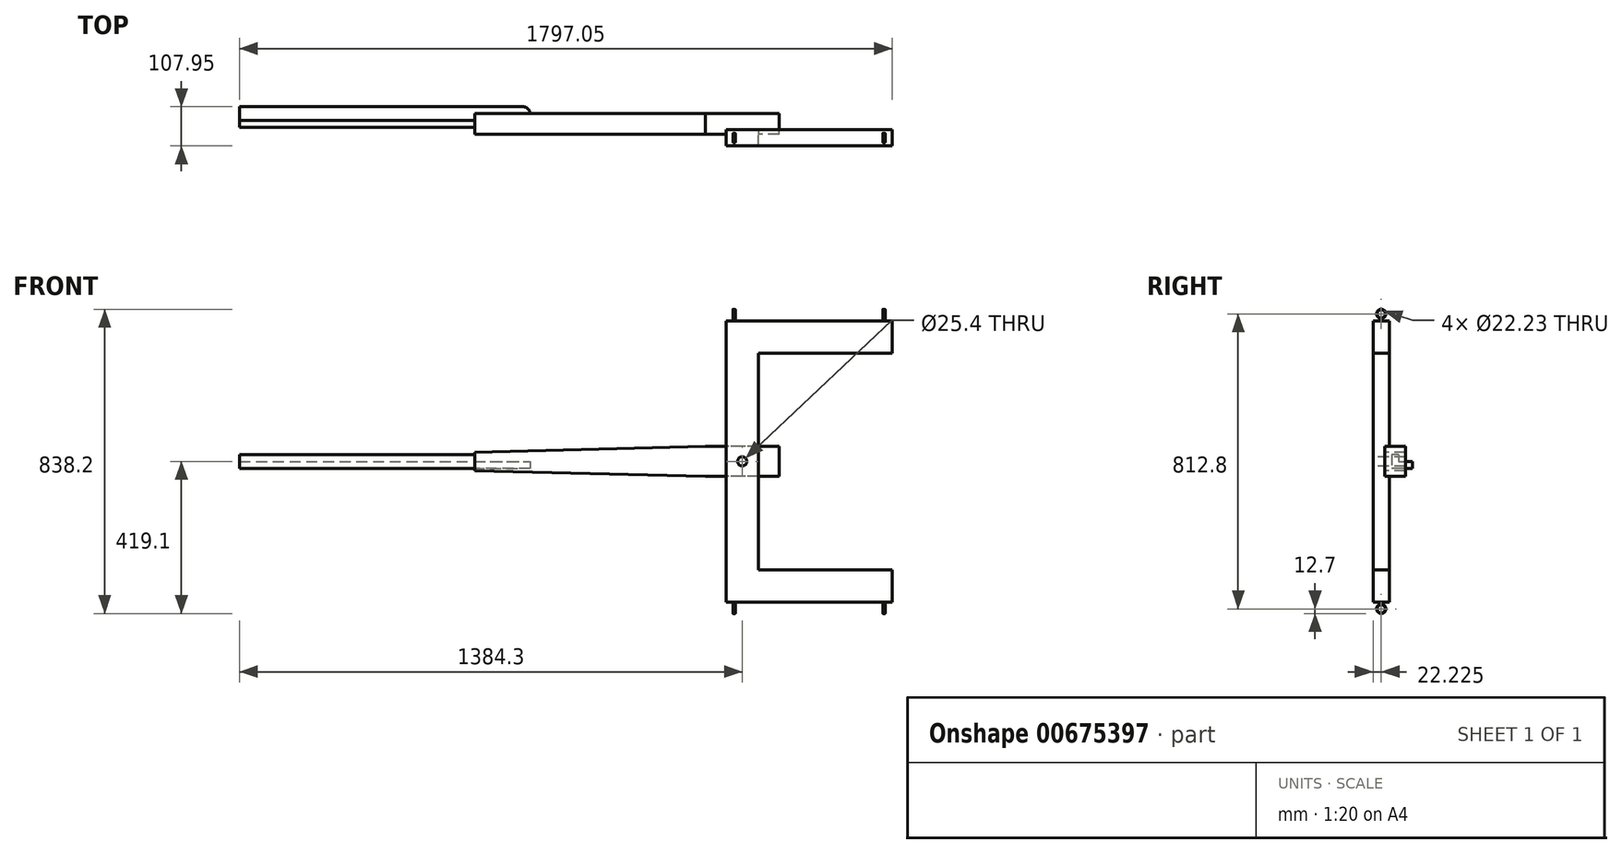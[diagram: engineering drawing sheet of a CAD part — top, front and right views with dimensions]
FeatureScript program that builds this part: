
annotation { "Feature Type Name" : "Feature", "Feature Type Description" : "" }
export const myFeature = defineFeature(function(context is Context, id is Id, definition is map)
    precondition{}
    {
        {
            var Q0;
            Q0=qCreatedBy(makeId("Front.planeOp"),FACE);
            var sketch = newSketch(context, id + "F0", { "sketchPlane" : qUnion([Q0])});
            skLineSegment(sketch, "E0.bottom", {"start": v(101.6, 41.27) * mm, "end": v(-736.6, 41.27) * mm});
            skLineSegment(sketch, "E0.top", {"start": v(101.6, -41.27) * mm, "end": v(-736.6, -41.28) * mm});
            skLineSegment(sketch, "E0.left", {"start": v(101.6, 41.28) * mm, "end": v(101.6, -41.27) * mm});
            skLineSegment(sketch, "E0.right", {"start": v(-736.6, 41.27) * mm, "end": v(-736.6, -41.28) * mm});
            skSolve(sketch);
        }
        {
            var Q0;
            Q0 = qSketchRegion(id + "F0", true);
            extrude(context, id + "F1", {"entities" : qUnion([Q0]), "depth" : 57.15 * mm, "offsetDistance" : 25.4 * mm});
        }
        {
            var Q0;
            Q0=makeQuery(id+"F1.opExtrude","CAP_FACE",FACE,{"disambiguationData":[OSD([sQuery(id+"F0.wireOp",EDGE,"E0.bottom"),sQuery(id+"F0.wireOp",EDGE,"E0.top"),sQuery(id+"F0.wireOp",EDGE,"E0.left"),sQuery(id+"F0.wireOp",EDGE,"E0.right")])],"isStart":false});
            var sketch = newSketch(context, id + "F2", { "sketchPlane" : qUnion([Q0])});
            skLineSegment(sketch, "E1", {"start": v(-736.6, 41.27) * mm, "end": v(-736.6, 25.4) * mm});
            skLineSegment(sketch, "E2", {"start": v(-736.6, 25.4) * mm, "end": v(-101.6, 41.27) * mm});
            skLineSegment(sketch, "E3", {"start": v(-101.6, 41.27) * mm, "end": v(-736.6, 41.27) * mm});
            skLineSegment(sketch, "E4", {"start": v(-736.6, -41.28) * mm, "end": v(-736.6, -25.4) * mm});
            skLineSegment(sketch, "E5", {"start": v(-736.6, -25.4) * mm, "end": v(-101.6, -41.27) * mm});
            skLineSegment(sketch, "E6", {"start": v(-101.6, -41.28) * mm, "end": v(-736.6, -41.28) * mm});
            skSolve(sketch);
        }
        {
            var Q0;
            Q0 = qSketchRegion(id + "F2", true);
            extrude(context, id + "F3", {"entities" : qUnion([Q0]), "operationType" : NewBodyOperationType.REMOVE, "endBound" : BoundingType.THROUGH_ALL, "oppositeDirection" : true, "depth" : 25.4 * mm, "offsetDistance" : 25.4 * mm});
        }
        {
            var Q0;
            Q0=makeQuery(id+"F1.opExtrude","CAP_FACE",FACE,{"disambiguationData":[OSD([sQuery(id+"F0.wireOp",EDGE,"E0.bottom"),sQuery(id+"F0.wireOp",EDGE,"E0.top"),sQuery(id+"F0.wireOp",EDGE,"E0.left"),sQuery(id+"F0.wireOp",EDGE,"E0.right")])],"isStart":false});
            var sketch = newSketch(context, id + "F4", { "sketchPlane" : qUnion([Q0])});
            skLineSegment(sketch, "E7.left", {"start": v(-44.45, 298.45) * mm, "end": v(-44.45, -298.45) * mm});
            skLineSegment(sketch, "E7.right", {"start": v(44.45, 298.45) * mm, "end": v(44.45, -298.45) * mm});
            skLineSegment(sketch, "E8.bottom", {"start": v(44.45, 298.45) * mm, "end": v(412.75, 298.45) * mm});
            skLineSegment(sketch, "E8.top", {"start": v(-44.45, 387.35) * mm, "end": v(412.75, 387.35) * mm});
            skLineSegment(sketch, "E8.left", {"start": v(-44.45, 298.45) * mm, "end": v(-44.45, 387.35) * mm});
            skLineSegment(sketch, "E8.right", {"start": v(412.75, 298.45) * mm, "end": v(412.75, 387.35) * mm});
            skLineSegment(sketch, "E9.bottom", {"start": v(44.45, -298.45) * mm, "end": v(412.75, -298.45) * mm});
            skLineSegment(sketch, "E9.top", {"start": v(-44.45, -387.35) * mm, "end": v(412.75, -387.35) * mm});
            skLineSegment(sketch, "E9.left", {"start": v(-44.45, -298.45) * mm, "end": v(-44.45, -387.35) * mm});
            skLineSegment(sketch, "E9.right", {"start": v(412.75, -298.45) * mm, "end": v(412.75, -387.35) * mm});
            skSolve(sketch);
        }
        {
            var Q0;
            {var subQ0=sQuery(id+"F4.wireOp",EDGE,"E8.bottom");Q0=makeQuery(id+"F4.imprint","IMPRINT",FACE,{"disambiguationData":[TD([[makeQuery(id+"F4.imprint","IMPRINT",EDGE,{"derivedFrom":subQ0}),1.0]])]});}
            var Q1;
            {var subQ0=sQuery(id+"F4.wireOp",EDGE,"E9.bottom");Q1=makeQuery(id+"F4.imprint","IMPRINT",FACE,{"disambiguationData":[TD([[makeQuery(id+"F4.imprint","IMPRINT",EDGE,{"derivedFrom":subQ0}),-1.0]])]});}
            var Q2;
            {var subQ0=sQuery(id+"F4.wireOp",EDGE,"E7.left");var subQ1=makeQuery(id+"F1.opExtrude","CAP_EDGE",EDGE,{"disambiguationData":[OSD([sQuery(id+"F0.wireOp",EDGE,"E0.bottom")])],"isStart":false});var subQ2=makeQuery(id+"F4.imprint","INTERSECT",VERTEX,{"derivedFrom":[subQ1,subQ0]});Q2=makeQuery(id+"F4.imprint","IMPRINT",FACE,{"disambiguationData":[TD([[makeQuery(id+"F4.imprint","IMPRINT",EDGE,{"disambiguationData":[TD([[subQ2,-1.0]])],"derivedFrom":subQ0}),1.0]])]});}
            extrude(context, id + "F5", {"entities" : qUnion([Q0, Q1, Q2]), "operationType" : NewBodyOperationType.ADD, "depth" : 31.75 * mm, "offsetDistance" : 25.4 * mm, "hasSecondDirection" : true, "secondDirectionOppositeDirection" : true, "secondDirectionDepth" : 12.7 * mm});
        }
        {
            var Q0;
            Q0=makeQuery(id+"F5.opExtrude","CAP_FACE",FACE,{"disambiguationData":[OSD([sQuery(id+"F4.wireOp",EDGE,"E7.left"),sQuery(id+"F4.wireOp",EDGE,"E7.right"),sQuery(id+"F4.wireOp",EDGE,"E8.bottom"),sQuery(id+"F4.wireOp",EDGE,"E8.top"),sQuery(id+"F4.wireOp",EDGE,"E8.left"),sQuery(id+"F4.wireOp",EDGE,"E8.right"),sQuery(id+"F4.wireOp",EDGE,"E9.bottom"),sQuery(id+"F4.wireOp",EDGE,"E9.top"),sQuery(id+"F4.wireOp",EDGE,"E9.left"),sQuery(id+"F4.wireOp",EDGE,"E9.right")])],"isStart":false});
            var sketch = newSketch(context, id + "F6", { "sketchPlane" : qUnion([Q0])});
            skCircle(sketch, "E10", {"center": v(0, 0) * mm, "radius": 12.7 * mm});
            skSolve(sketch);
        }
        {
            var Q0;
            Q0 = qSketchRegion(id + "F6", true);
            extrude(context, id + "F7", {"entities" : qUnion([Q0]), "operationType" : NewBodyOperationType.REMOVE, "endBound" : BoundingType.THROUGH_ALL, "oppositeDirection" : true, "depth" : 25.4 * mm, "offsetDistance" : 25.4 * mm});
        }
        {
            var Q0;
            Q0=makeQuery(id+"F1.opExtrude","SWEPT_FACE",FACE,{"disambiguationData":[OSD([sQuery(id+"F0.wireOp",EDGE,"E0.right")])]});
            var sketch = newSketch(context, id + "F8", { "sketchPlane" : qUnion([Q0])});
            skLineSegment(sketch, "E11.bottom", {"start": v(19.05, 19.05) * mm, "end": v(38.1, 19.05) * mm});
            skLineSegment(sketch, "E11.top", {"start": v(19.05, -19.05) * mm, "end": v(38.1, -19.05) * mm});
            skLineSegment(sketch, "E11.left", {"start": v(19.05, 19.05) * mm, "end": v(19.05, -19.05) * mm});
            skLineSegment(sketch, "E11.right", {"start": v(38.1, 19.05) * mm, "end": v(38.1, -19.05) * mm});
            skLineSegment(sketch, "E12.left", {"start": v(38.1, 19.05) * mm, "end": v(38.1, 0) * mm});
            skLineSegment(sketch, "E13.bottom", {"start": v(19.05, -19.05) * mm, "end": v(-19.05, -19.05) * mm});
            skLineSegment(sketch, "E13.top", {"start": v(19.05, 0) * mm, "end": v(-19.05, 0) * mm});
            skLineSegment(sketch, "E13.left", {"start": v(19.05, -19.05) * mm, "end": v(19.05, 0) * mm});
            skLineSegment(sketch, "E13.right", {"start": v(-19.05, -19.05) * mm, "end": v(-19.05, 0) * mm});
            skSolve(sketch);
        }
        {
            var Q0;
            Q0 = qSketchRegion(id + "F8", true);
            extrude(context, id + "F9", {"entities" : qUnion([Q0]), "operationType" : NewBodyOperationType.ADD, "depth" : 647.7 * mm, "offsetDistance" : 25.4 * mm, "hasSecondDirection" : true, "secondDirectionOppositeDirection" : true, "secondDirectionDepth" : 152.4 * mm});
        }
        {
            var Q0;
            Q0=makeQuery(id+"F5.opExtrude","SWEPT_FACE",FACE,{"disambiguationData":[OSD([sQuery(id+"F4.wireOp",EDGE,"E8.right")])]});
            var sketch = newSketch(context, id + "F10", { "sketchPlane" : qUnion([Q0])});
            skCircle(sketch, "E14", {"center": v(-66.68, 406.4) * mm, "radius": 11.11 * mm});
            skArc(sketch, "E15", {"start": v(-63.5, 394.1) * mm, "mid": v(-66.68, 419.1) * mm, "end": v(-69.85, 394.1) * mm});
            skLineSegment(sketch, "E16.top", {"start": v(-69.85, 368.3) * mm, "end": v(-63.5, 368.3) * mm});
            skLineSegment(sketch, "E16.left", {"start": v(-69.85, 394.1) * mm, "end": v(-69.85, 368.3) * mm});
            skLineSegment(sketch, "E16.right", {"start": v(-63.5, 394.1) * mm, "end": v(-63.5, 368.3) * mm});
            skSolve(sketch);
        }
        {
            var Q0;
            Q0 = qSketchRegion(id + "F10", true);
            extrude(context, id + "F11", {"entities" : qUnion([Q0]), "operationType" : NewBodyOperationType.ADD, "oppositeDirection" : true, "depth" : 25.4 * mm, "offsetDistance" : 25.4 * mm, "hasSecondDirection" : true, "secondDirectionOppositeDirection" : true, "secondDirectionDepth" : 19.05 * mm});
        }
        {
            var Q0;
            Q0=makeQuery(id+"F11.opExtrude","CAP_EDGE",EDGE,{"disambiguationData":[OSD([sQuery(id+"F10.wireOp",EDGE,"E16.right")])],"isStart":true});
            var Q1;
            Q1=makeQuery(id+"F11.opExtrude","CAP_EDGE",EDGE,{"disambiguationData":[OSD([sQuery(id+"F10.wireOp",EDGE,"E16.right")])],"isStart":false});
            var Q2;
            Q2=makeQuery(id+"F11.opExtrude","CAP_EDGE",EDGE,{"disambiguationData":[OSD([sQuery(id+"F10.wireOp",EDGE,"E16.left")])],"isStart":true});
            var Q3;
            Q3=makeQuery(id+"F11.opExtrude","CAP_EDGE",EDGE,{"disambiguationData":[OSD([sQuery(id+"F10.wireOp",EDGE,"E16.left")])],"isStart":false});
            fillet(context, id + "F12", {"entities" : qUnion([Q0, Q1, Q2, Q3]), "radius" : 3.17 * mm, "tangentPropagation" : true, "allowEdgeOverflow" : false});
        }
        {
            var Q0;
            Q0=makeQuery(id+"F11.opExtrude","CAP_EDGE",EDGE,{"disambiguationData":[OSD([sQuery(id+"F10.wireOp",EDGE,"E15")])],"isStart":false});
            var Q1;
            Q1=makeQuery(id+"F11.opExtrude","CAP_EDGE",EDGE,{"disambiguationData":[OSD([sQuery(id+"F10.wireOp",EDGE,"E14")])],"isStart":false});
            var Q2;
            Q2=makeQuery(id+"F11.opExtrude","CAP_EDGE",EDGE,{"disambiguationData":[OSD([sQuery(id+"F10.wireOp",EDGE,"E15")])],"isStart":true});
            var Q3;
            Q3=makeQuery(id+"F11.opExtrude","CAP_EDGE",EDGE,{"disambiguationData":[OSD([sQuery(id+"F10.wireOp",EDGE,"E14")])],"isStart":true});
            fillet(context, id + "F13", {"entities" : qUnion([Q0, Q1, Q2, Q3]), "radius" : 0.64 * mm, "tangentPropagation" : true, "allowEdgeOverflow" : false});
        }
        {
            var Q0;
            Q0=makeQuery(id+"F5.opExtrude","SWEPT_FACE",FACE,{"disambiguationData":[OSD([sQuery(id+"F4.wireOp",EDGE,"E7.left"),sQuery(id+"F4.wireOp",EDGE,"E8.left"),sQuery(id+"F4.wireOp",EDGE,"E9.left")])]});
            var sketch = newSketch(context, id + "F14", { "sketchPlane" : qUnion([Q0])});
            skCircle(sketch, "E17", {"center": v(66.68, 406.4) * mm, "radius": 11.11 * mm});
            skArc(sketch, "E18", {"start": v(69.85, 394.1) * mm, "mid": v(66.68, 419.1) * mm, "end": v(63.5, 394.1) * mm});
            skLineSegment(sketch, "E19.top", {"start": v(63.5, 368.3) * mm, "end": v(69.85, 368.3) * mm});
            skLineSegment(sketch, "E19.left", {"start": v(63.5, 394.1) * mm, "end": v(63.5, 368.3) * mm});
            skLineSegment(sketch, "E19.right", {"start": v(69.85, 394.1) * mm, "end": v(69.85, 368.3) * mm});
            skSolve(sketch);
        }
        {
            var Q0;
            Q0 = qSketchRegion(id + "F14", true);
            extrude(context, id + "F15", {"entities" : qUnion([Q0]), "operationType" : NewBodyOperationType.ADD, "oppositeDirection" : true, "depth" : 25.4 * mm, "offsetDistance" : 25.4 * mm, "hasSecondDirection" : true, "secondDirectionOppositeDirection" : true, "secondDirectionDepth" : 19.05 * mm});
        }
        {
            var Q0;
            Q0=makeQuery(id+"F15.opExtrude","CAP_EDGE",EDGE,{"disambiguationData":[OSD([sQuery(id+"F14.wireOp",EDGE,"E19.right")])],"isStart":true});
            var Q1;
            Q1=makeQuery(id+"F15.opExtrude","CAP_EDGE",EDGE,{"disambiguationData":[OSD([sQuery(id+"F14.wireOp",EDGE,"E19.right")])],"isStart":false});
            var Q2;
            Q2=makeQuery(id+"F15.opExtrude","CAP_EDGE",EDGE,{"disambiguationData":[OSD([sQuery(id+"F14.wireOp",EDGE,"E19.left")])],"isStart":true});
            var Q3;
            Q3=makeQuery(id+"F15.opExtrude","CAP_EDGE",EDGE,{"disambiguationData":[OSD([sQuery(id+"F14.wireOp",EDGE,"E19.left")])],"isStart":false});
            fillet(context, id + "F16", {"entities" : qUnion([Q0, Q1, Q2, Q3]), "radius" : 3.17 * mm, "tangentPropagation" : true, "allowEdgeOverflow" : false});
        }
        {
            var Q0;
            Q0=makeQuery(id+"F15.opExtrude","CAP_EDGE",EDGE,{"disambiguationData":[OSD([sQuery(id+"F14.wireOp",EDGE,"E18")])],"isStart":false});
            var Q1;
            Q1=makeQuery(id+"F15.opExtrude","CAP_EDGE",EDGE,{"disambiguationData":[OSD([sQuery(id+"F14.wireOp",EDGE,"E18")])],"isStart":true});
            var Q2;
            Q2=makeQuery(id+"F15.opExtrude","CAP_EDGE",EDGE,{"disambiguationData":[OSD([sQuery(id+"F14.wireOp",EDGE,"E17")])],"isStart":true});
            var Q3;
            Q3=makeQuery(id+"F15.opExtrude","CAP_EDGE",EDGE,{"disambiguationData":[OSD([sQuery(id+"F14.wireOp",EDGE,"E17")])],"isStart":false});
            fillet(context, id + "F17", {"entities" : qUnion([Q0, Q1, Q2, Q3]), "radius" : 0.64 * mm, "tangentPropagation" : true, "allowEdgeOverflow" : false});
        }
        {
            var Q0;
            Q0=makeQuery(id+"F5.opExtrude","SWEPT_FACE",FACE,{"disambiguationData":[OSD([sQuery(id+"F4.wireOp",EDGE,"E9.right")])]});
            var sketch = newSketch(context, id + "F18", { "sketchPlane" : qUnion([Q0])});
            skArc(sketch, "E20.MirrorCS", {"start": v(-63.5, -394.1) * mm, "mid": v(-66.68, -419.1) * mm, "end": v(-69.85, -394.1) * mm});
            skLineSegment(sketch, "E21.MirrorCS", {"start": v(-69.85, -368.3) * mm, "end": v(-63.5, -368.3) * mm});
            skLineSegment(sketch, "E22.MirrorCS", {"start": v(-69.85, -394.1) * mm, "end": v(-69.85, -368.3) * mm});
            skLineSegment(sketch, "E23.MirrorCS", {"start": v(-63.5, -394.1) * mm, "end": v(-63.5, -368.3) * mm});
            skCircle(sketch, "E24.MirrorC", {"center": v(-66.68, -406.4) * mm, "radius": 11.11 * mm});
            skSolve(sketch);
        }
        {
            var Q0;
            Q0 = qSketchRegion(id + "F18", true);
            extrude(context, id + "F19", {"entities" : qUnion([Q0]), "operationType" : NewBodyOperationType.ADD, "oppositeDirection" : true, "depth" : 25.4 * mm, "offsetDistance" : 25.4 * mm, "hasSecondDirection" : true, "secondDirectionOppositeDirection" : true, "secondDirectionDepth" : 19.05 * mm});
        }
        {
            var Q0;
            Q0=makeQuery(id+"F19.opExtrude","CAP_EDGE",EDGE,{"disambiguationData":[OSD([sQuery(id+"F18.wireOp",EDGE,"E23.MirrorCS")])],"isStart":true});
            var Q1;
            Q1=makeQuery(id+"F19.opExtrude","CAP_EDGE",EDGE,{"disambiguationData":[OSD([sQuery(id+"F18.wireOp",EDGE,"E22.MirrorCS")])],"isStart":true});
            var Q2;
            Q2=makeQuery(id+"F19.opExtrude","CAP_EDGE",EDGE,{"disambiguationData":[OSD([sQuery(id+"F18.wireOp",EDGE,"E23.MirrorCS")])],"isStart":false});
            var Q3;
            Q3=makeQuery(id+"F19.opExtrude","CAP_EDGE",EDGE,{"disambiguationData":[OSD([sQuery(id+"F18.wireOp",EDGE,"E22.MirrorCS")])],"isStart":false});
            fillet(context, id + "F20", {"entities" : qUnion([Q0, Q1, Q2, Q3]), "radius" : 3.17 * mm, "tangentPropagation" : true, "allowEdgeOverflow" : false});
        }
        {
            var Q0;
            Q0=makeQuery(id+"F19.opExtrude","CAP_EDGE",EDGE,{"disambiguationData":[OSD([sQuery(id+"F18.wireOp",EDGE,"E24.MirrorC")])],"isStart":true});
            var Q1;
            Q1=makeQuery(id+"F19.opExtrude","CAP_EDGE",EDGE,{"disambiguationData":[OSD([sQuery(id+"F18.wireOp",EDGE,"E20.MirrorCS")])],"isStart":true});
            var Q2;
            Q2=makeQuery(id+"F19.opExtrude","CAP_EDGE",EDGE,{"disambiguationData":[OSD([sQuery(id+"F18.wireOp",EDGE,"E20.MirrorCS")])],"isStart":false});
            var Q3;
            Q3=makeQuery(id+"F19.opExtrude","CAP_EDGE",EDGE,{"disambiguationData":[OSD([sQuery(id+"F18.wireOp",EDGE,"E24.MirrorC")])],"isStart":false});
            fillet(context, id + "F21", {"entities" : qUnion([Q0, Q1, Q2, Q3]), "radius" : 0.64 * mm, "tangentPropagation" : true, "allowEdgeOverflow" : false});
        }
        {
            var Q0;
            Q0=makeQuery(id+"F5.opExtrude","SWEPT_FACE",FACE,{"disambiguationData":[OSD([sQuery(id+"F4.wireOp",EDGE,"E7.left"),sQuery(id+"F4.wireOp",EDGE,"E8.left"),sQuery(id+"F4.wireOp",EDGE,"E9.left")])]});
            var sketch = newSketch(context, id + "F22", { "sketchPlane" : qUnion([Q0])});
            skArc(sketch, "E25.MirrorCS", {"start": v(69.85, -394.1) * mm, "mid": v(66.68, -419.1) * mm, "end": v(63.5, -394.1) * mm});
            skLineSegment(sketch, "E26.MirrorCS", {"start": v(63.5, -368.3) * mm, "end": v(69.85, -368.3) * mm});
            skLineSegment(sketch, "E27.MirrorCS", {"start": v(63.5, -394.1) * mm, "end": v(63.5, -368.3) * mm});
            skLineSegment(sketch, "E28.MirrorCS", {"start": v(69.85, -394.1) * mm, "end": v(69.85, -368.3) * mm});
            skCircle(sketch, "E29.MirrorC", {"center": v(66.68, -406.4) * mm, "radius": 11.11 * mm});
            skSolve(sketch);
        }
        {
            var Q0;
            Q0 = qSketchRegion(id + "F22", true);
            extrude(context, id + "F23", {"entities" : qUnion([Q0]), "operationType" : NewBodyOperationType.ADD, "oppositeDirection" : true, "depth" : 25.4 * mm, "offsetDistance" : 25.4 * mm, "hasSecondDirection" : true, "secondDirectionOppositeDirection" : true, "secondDirectionDepth" : 19.05 * mm});
        }
        {
            var Q0;
            Q0=makeQuery(id+"F23.opExtrude","CAP_EDGE",EDGE,{"disambiguationData":[OSD([sQuery(id+"F22.wireOp",EDGE,"E28.MirrorCS")])],"isStart":true});
            var Q1;
            Q1=makeQuery(id+"F23.opExtrude","CAP_EDGE",EDGE,{"disambiguationData":[OSD([sQuery(id+"F22.wireOp",EDGE,"E27.MirrorCS")])],"isStart":true});
            var Q2;
            Q2=makeQuery(id+"F23.opExtrude","CAP_EDGE",EDGE,{"disambiguationData":[OSD([sQuery(id+"F22.wireOp",EDGE,"E28.MirrorCS")])],"isStart":false});
            var Q3;
            Q3=makeQuery(id+"F23.opExtrude","CAP_EDGE",EDGE,{"disambiguationData":[OSD([sQuery(id+"F22.wireOp",EDGE,"E27.MirrorCS")])],"isStart":false});
            fillet(context, id + "F24", {"entities" : qUnion([Q0, Q1, Q2, Q3]), "radius" : 3.17 * mm, "tangentPropagation" : true, "allowEdgeOverflow" : false});
        }
        {
            var Q0;
            Q0=makeQuery(id+"F23.opExtrude","CAP_EDGE",EDGE,{"disambiguationData":[OSD([sQuery(id+"F22.wireOp",EDGE,"E25.MirrorCS")])],"isStart":true});
            var Q1;
            Q1=makeQuery(id+"F23.opExtrude","CAP_EDGE",EDGE,{"disambiguationData":[OSD([sQuery(id+"F22.wireOp",EDGE,"E29.MirrorC")])],"isStart":true});
            var Q2;
            Q2=makeQuery(id+"F23.opExtrude","CAP_EDGE",EDGE,{"disambiguationData":[OSD([sQuery(id+"F22.wireOp",EDGE,"E29.MirrorC")])],"isStart":false});
            var Q3;
            Q3=makeQuery(id+"F23.opExtrude","CAP_EDGE",EDGE,{"disambiguationData":[OSD([sQuery(id+"F22.wireOp",EDGE,"E25.MirrorCS")])],"isStart":false});
            fillet(context, id + "F25", {"entities" : qUnion([Q0, Q1, Q2, Q3]), "radius" : 0.64 * mm, "tangentPropagation" : true, "allowEdgeOverflow" : false});
        }
        {
            var Q0;
            Q0=makeQuery(id+"F9.opExtrude","CAP_EDGE",EDGE,{"disambiguationData":[OSD([sQuery(id+"F8.wireOp",EDGE,"E13.right")])],"isStart":true});
            fillet(context, id + "F26", {"entities" : qUnion([Q0]), "radius" : 19.05 * mm, "tangentPropagation" : true, "allowEdgeOverflow" : false});
        }
    });
